# Revit family: Hawle_Задвижка 4000А_DN80-DN300
name_source: partatom
category: Арматура трубопроводов
revit_build: Autodesk Revit 2017 (Build: 20171027_0315(x64)
units: mm (PartAtom-declared; Revit-internal decimal feet)

## family parameters
Всегда вертикально = Да
На основе рабочей плоскости = Нет
Общий = Нет
При загрузке вырезать с полостями = Нет
Размер круглого соединителя = Использовать диаметр
Тип детали = Вставляется

## types (1)
- Hawle_Задвижка 4000А_DN80-DN300
    ADSK_Единица измерения = Шт.
    ADSK_Завод-изготовитель = Hawle
    ADSK_Код изделия = 4000А
    ADSK_Обозначение = EN 558-1 GR14
    Bolt = Bolt
    Disc = Disc
    URL = https://www.hawle.ru
    Изготовитель = ООО Хавле-Севком
    Изготовитель телефон = +7(812)6707670
    Материал_Корпус = Hawle_Чугун
    Материал_Пыльник = Hawle_PE
    Материал_Фланцы = Hawle_Нержавеющая сталь
    Материал_Шпиндель = Hawle_Нержавеющая сталь
    Описание = Упругозапирающаяся клиновая задвижка со свободным проходным каналом
    Разработчик = ООО ПРОРУБИМ
    Разработчик (телефон) = +7(495)649-85-43
    Разработчик модели (URL) = http://prorubim.com
    Таблица размеры = Hawle_Задвижка 4000А_DN80-DN300_размеры
